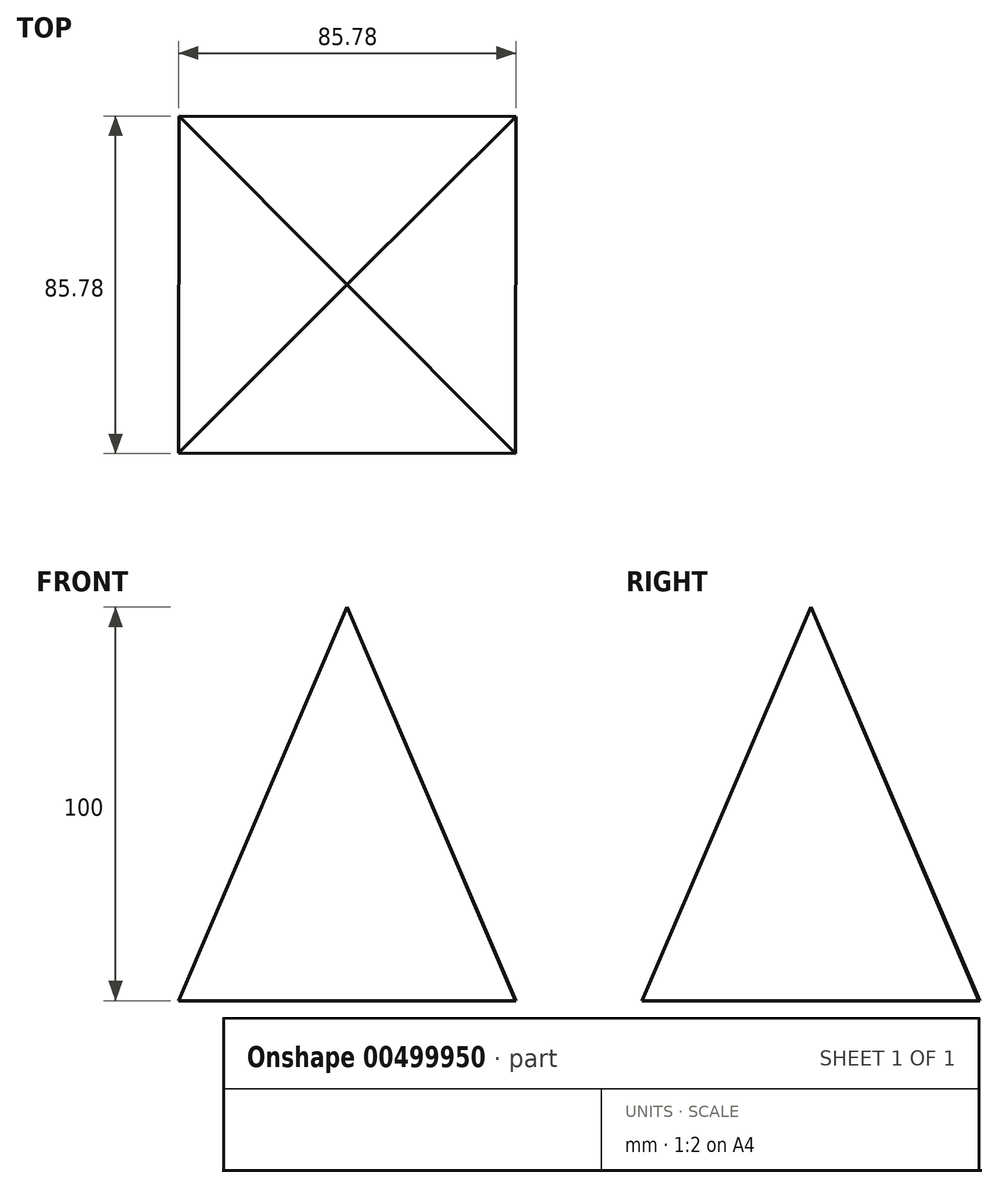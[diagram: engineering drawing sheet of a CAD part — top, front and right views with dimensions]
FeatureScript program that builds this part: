
annotation { "Feature Type Name" : "Feature", "Feature Type Description" : "" }
export const myFeature = defineFeature(function(context is Context, id is Id, definition is map)
    precondition{}
    {
        {
            var Q0;
            Q0=qCreatedBy(makeId("Top.planeOp"),FACE);
            var sketch = newSketch(context, id + "F0", { "sketchPlane" : qUnion([Q0])});
            skCircle(sketch, "E0.cCircle", {"center": v(0, 0) * mm, "radius": 60.55 * mm, "construction": true});
            skLineSegment(sketch, "E0.0", {"start": v(-42.75, 42.89) * mm, "end": v(42.89, 42.75) * mm});
            skLineSegment(sketch, "E0.1", {"start": v(42.89, 42.75) * mm, "end": v(42.75, -42.89) * mm});
            skLineSegment(sketch, "E0.2", {"start": v(42.75, -42.89) * mm, "end": v(-42.89, -42.75) * mm});
            skLineSegment(sketch, "E0.3", {"start": v(-42.89, -42.75) * mm, "end": v(-42.75, 42.89) * mm});
            skSolve(sketch);
        }
        {
            var Q0;
            Q0=qCreatedBy(makeId("Top.planeOp"),FACE);
            cPlane(context, id + "F1", {"entities" : qUnion([Q0]), "cplaneType" : CPlaneType.OFFSET, "offset" : 100 * mm, "width" : 150 * mm, "height" : 150 * mm});
        }
        {
            var Q0;
            Q0=qCreatedBy(id+"F1.planeOp",FACE);
            var sketch = newSketch(context, id + "F2", { "sketchPlane" : qUnion([Q0])});
            skPoint(sketch, "E1", {"position": v(0, 0) * mm});
            skSolve(sketch);
        }
        {
            var Q0;
            Q0=makeQuery(id+"F0.imprint","IMPRINT",FACE,{"disambiguationData":[TD([[makeQuery(id+"F0.imprint","IMPRINT",EDGE,{"derivedFrom":sQuery(id+"F0.wireOp",EDGE,"E0.0")}),-1.0]])]});
            var Q1;
            Q1=sQuery(id+"F2.wireOp",VERTEX,"E1");
            loft(context, id + "F3", {"sheetProfilesArray" : [{ "sheetProfileEntities" : qUnion([Q0]) }, { "sheetProfileEntities" : qUnion([Q1]) }]});
        }
    });
